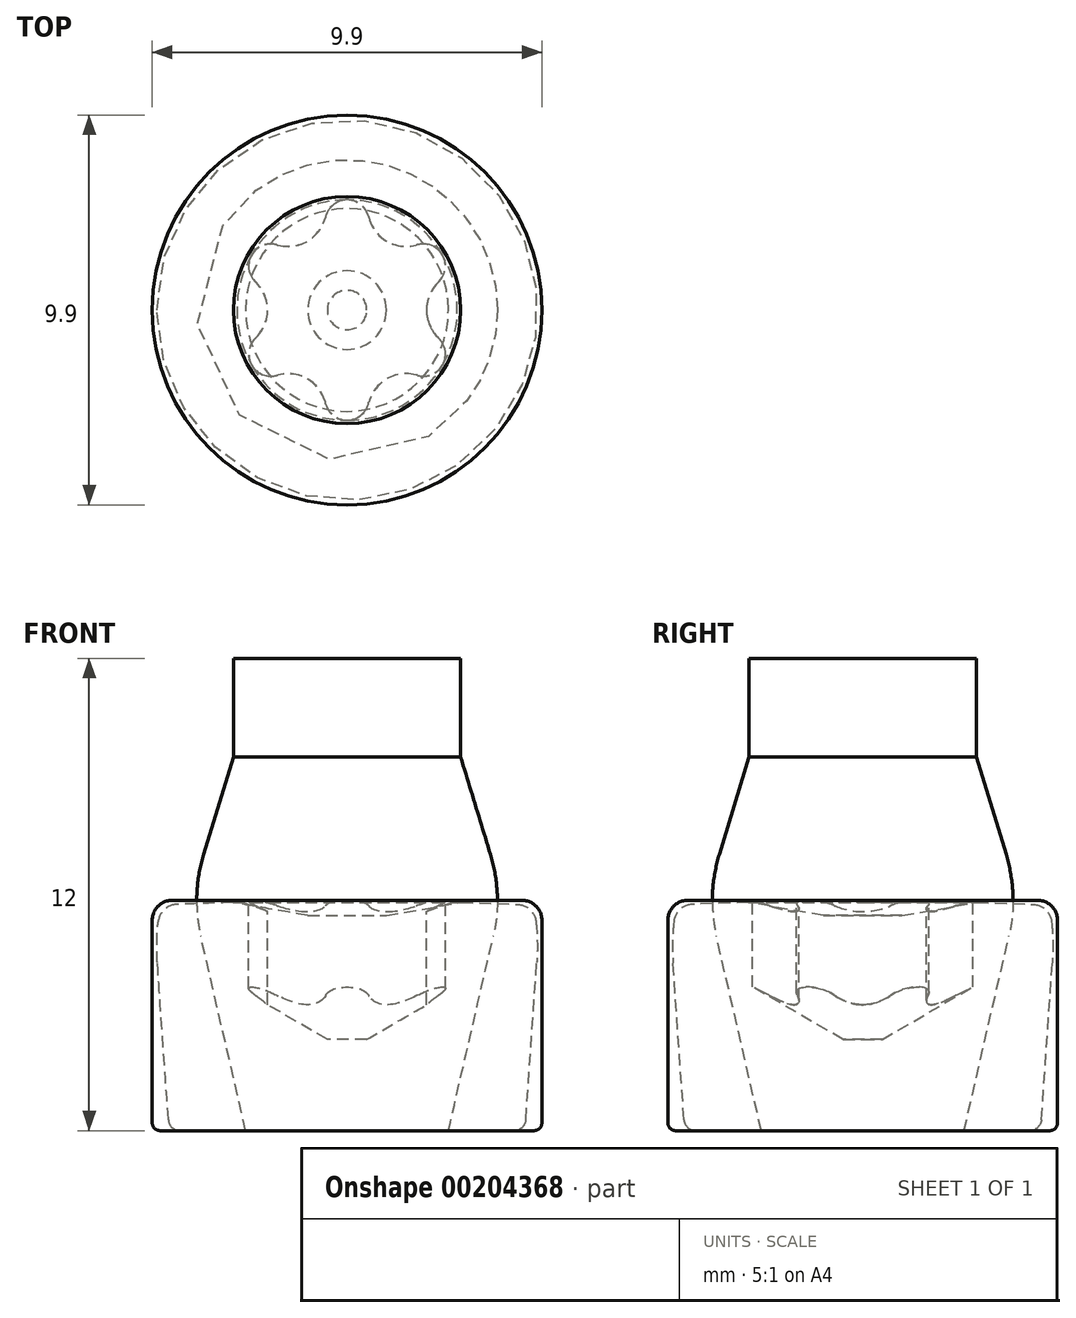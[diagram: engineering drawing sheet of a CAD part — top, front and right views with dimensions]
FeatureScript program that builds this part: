
annotation { "Feature Type Name" : "Feature", "Feature Type Description" : "" }
export const myFeature = defineFeature(function(context is Context, id is Id, definition is map)
    precondition{}
    {
        {
            var Q0;
            Q0=qCreatedBy(makeId("Front.planeOp"),FACE);
            var sketch = newSketch(context, id + "F0", { "sketchPlane" : qUnion([Q0])});
            skLineSegment(sketch, "E0", {"start": v(0, 0) * mm, "end": v(0, 2.32) * mm, "construction": true});
            skLineSegment(sketch, "E1", {"start": v(2.8, 5.85) * mm, "end": v(4.45, 5.85) * mm});
            skLineSegment(sketch, "E2", {"start": v(4.95, 5.35) * mm, "end": v(4.95, 0.2) * mm});
            skLineSegment(sketch, "E3", {"start": v(4.75, 0) * mm, "end": v(0, 0) * mm});
            skPoint(sketch, "E4.visualSharp", {"position": v(4.95, 5.85) * mm});
            skArc(sketch, "E4.filletArc", {"start": v(4.95, 5.35) * mm, "mid": v(4.8, 5.7) * mm, "end": v(4.45, 5.85) * mm});
            skPoint(sketch, "E5.visualSharp", {"position": v(4.95, 0) * mm});
            skArc(sketch, "E5.filletArc", {"start": v(4.75, 0) * mm, "mid": v(4.9, 0.06) * mm, "end": v(4.95, 0.2) * mm});
            skLineSegment(sketch, "E6", {"start": v(2.8, 5.85) * mm, "end": v(2.8, 3.65) * mm});
            skLineSegment(sketch, "E7", {"start": v(2.8, 3.65) * mm, "end": v(0.5, 2.32) * mm});
            skLineSegment(sketch, "E8", {"start": v(0.5, 2.32) * mm, "end": v(0, 2.32) * mm});
            skLineSegment(sketch, "E9", {"start": v(0, 2.32) * mm, "end": v(0, 0) * mm});
            skSolve(sketch);
        }
        {
            var Q0;
            Q0=qSketchRegion(id+"F0",true);
            var Q1;
            Q1=sQuery(id+"F0.wireOp",EDGE,"E9");
            revolve(context, id + "F1", {"entities" : qUnion([Q0]), "axis" : qUnion([Q1]), "revolveType" : RevolveType.FULL});
        }
        {
            var Q0;
            Q0=makeQuery(id+"F1.opRevolve","SWEPT_FACE",FACE,{"disambiguationData":[OSD([sQuery(id+"F0.wireOp",EDGE,"E1")])]});
            var sketch = newSketch(context, id + "F2", { "sketchPlane" : qUnion([Q0])});
            skArc(sketch, "E10", {"start": v(0.54, 2.38) * mm, "mid": v(0, 2.8) * mm, "end": v(-0.54, 2.38) * mm});
            skLineSegment(sketch, "E11", {"start": v(-0.54, 2.38) * mm, "end": v(-0.55, 2.34) * mm});
            skLineSegment(sketch, "E12", {"start": v(0.54, 2.38) * mm, "end": v(0.55, 2.34) * mm});
            skLineSegment(sketch, "E13.1.0", {"start": v(-1.8, 1.66) * mm, "end": v(-1.75, 1.65) * mm});
            skArc(sketch, "E13.1.1", {"start": v(-1.8, 1.66) * mm, "mid": v(-2.42, 1.4) * mm, "end": v(-2.34, 0.72) * mm});
            skLineSegment(sketch, "E13.1.2", {"start": v(-2.34, 0.72) * mm, "end": v(-2.3, 0.7) * mm});
            skLineSegment(sketch, "E13.2.0", {"start": v(-2.34, -0.72) * mm, "end": v(-2.3, -0.7) * mm});
            skArc(sketch, "E13.2.1", {"start": v(-2.34, -0.72) * mm, "mid": v(-2.42, -1.4) * mm, "end": v(-1.8, -1.66) * mm});
            skLineSegment(sketch, "E13.2.2", {"start": v(-1.8, -1.66) * mm, "end": v(-1.75, -1.65) * mm});
            skLineSegment(sketch, "E13.3.0", {"start": v(-0.54, -2.38) * mm, "end": v(-0.55, -2.34) * mm});
            skArc(sketch, "E13.3.1", {"start": v(-0.54, -2.38) * mm, "mid": v(0, -2.8) * mm, "end": v(0.54, -2.38) * mm});
            skLineSegment(sketch, "E13.3.2", {"start": v(0.54, -2.38) * mm, "end": v(0.55, -2.34) * mm});
            skLineSegment(sketch, "E13.4.0", {"start": v(1.8, -1.66) * mm, "end": v(1.75, -1.65) * mm});
            skArc(sketch, "E13.4.1", {"start": v(1.8, -1.66) * mm, "mid": v(2.42, -1.4) * mm, "end": v(2.34, -0.72) * mm});
            skLineSegment(sketch, "E13.4.2", {"start": v(2.34, -0.72) * mm, "end": v(2.3, -0.7) * mm});
            skLineSegment(sketch, "E13.5.0", {"start": v(2.34, 0.72) * mm, "end": v(2.3, 0.7) * mm});
            skArc(sketch, "E13.5.1", {"start": v(2.34, 0.72) * mm, "mid": v(2.42, 1.4) * mm, "end": v(1.8, 1.66) * mm});
            skLineSegment(sketch, "E13.5.2", {"start": v(1.8, 1.66) * mm, "end": v(1.75, 1.65) * mm});
            skPoint(sketch, "E13.center", {"position": v(0, 0) * mm});
            skPoint(sketch, "E14.newPointA", {"position": v(1.38, 0.81) * mm});
            skPoint(sketch, "E14.newPointB", {"position": v(-1.4, -0.8) * mm});
            skArc(sketch, "E14.filletArc", {"start": v(-1.75, 1.65) * mm, "mid": v(-1, 1.75) * mm, "end": v(-0.55, 2.34) * mm});
            skPoint(sketch, "E15.newPointA", {"position": v(-1.38, 0.8) * mm});
            skPoint(sketch, "E15.newPointB", {"position": v(1.4, -0.79) * mm});
            skArc(sketch, "E15.filletArc", {"start": v(0.55, 2.34) * mm, "mid": v(1, 1.75) * mm, "end": v(1.75, 1.65) * mm});
            skPoint(sketch, "E16.newPointA", {"position": v(0.01, -1.6) * mm});
            skPoint(sketch, "E16.newPointB", {"position": v(0, 1.6) * mm});
            skArc(sketch, "E16.filletArc", {"start": v(2.3, 0.7) * mm, "mid": v(2.02, 0) * mm, "end": v(2.3, -0.7) * mm});
            skPoint(sketch, "E17.newPointA", {"position": v(-1.38, -0.81) * mm});
            skPoint(sketch, "E17.newPointB", {"position": v(1.4, 0.8) * mm});
            skArc(sketch, "E17.filletArc", {"start": v(1.75, -1.65) * mm, "mid": v(1, -1.75) * mm, "end": v(0.55, -2.34) * mm});
            skPoint(sketch, "E18.newPointA", {"position": v(-1.4, 0.79) * mm});
            skPoint(sketch, "E18.newPointB", {"position": v(1.38, -0.8) * mm});
            skArc(sketch, "E18.filletArc", {"start": v(-0.55, -2.34) * mm, "mid": v(-1, -1.75) * mm, "end": v(-1.75, -1.65) * mm});
            skPoint(sketch, "E19.newPointA", {"position": v(-0.01, 1.6) * mm});
            skPoint(sketch, "E19.newPointB", {"position": v(0, -1.6) * mm});
            skArc(sketch, "E19.filletArc", {"start": v(-2.3, -0.7) * mm, "mid": v(-2.02, 0) * mm, "end": v(-2.3, 0.7) * mm});
            skCircle(sketch, "E20", {"center": v(0, 0) * mm, "radius": 3 * mm});
            skSolve(sketch);
        }
        {
            var Q0;
            Q0=qSketchRegion(id+"F2",true);
            var Q1;
            Q1=makeQuery(id+"F1.opRevolve","SWEPT_FACE",FACE,{"disambiguationData":[OSD([sQuery(id+"F0.wireOp",EDGE,"E7")])]});
            extrude(context, id + "F3", {"entities" : qUnion([Q0]), "operationType" : NewBodyOperationType.ADD, "endBound" : BoundingType.UP_TO_SURFACE, "oppositeDirection" : true, "endBoundEntityFace" : qUnion([Q1]), "depth" : 25 * mm, "offsetDistance" : 25 * mm});
        }
        {
            var Q0;
            Q0=makeQuery(id+"F3.boolean.opBoolean","MERGE",FACE,{"derivedFrom":[makeQuery(id+"F1.opRevolve","SWEPT_FACE",FACE,{"disambiguationData":[OSD([sQuery(id+"F0.wireOp",EDGE,"E1")])]}),makeQuery(id+"F3.opExtrude","CAP_FACE",FACE,{"disambiguationData":[OSD([sQuery(id+"F2.wireOp",EDGE,"E10"),sQuery(id+"F2.wireOp",EDGE,"E11"),sQuery(id+"F2.wireOp",EDGE,"E12"),sQuery(id+"F2.wireOp",EDGE,"E13.1.0"),sQuery(id+"F2.wireOp",EDGE,"E13.1.1"),sQuery(id+"F2.wireOp",EDGE,"E13.1.2"),sQuery(id+"F2.wireOp",EDGE,"E13.2.0"),sQuery(id+"F2.wireOp",EDGE,"E13.2.1"),sQuery(id+"F2.wireOp",EDGE,"E13.2.2"),sQuery(id+"F2.wireOp",EDGE,"E13.3.0"),sQuery(id+"F2.wireOp",EDGE,"E13.3.1"),sQuery(id+"F2.wireOp",EDGE,"E13.3.2"),sQuery(id+"F2.wireOp",EDGE,"E13.4.0"),sQuery(id+"F2.wireOp",EDGE,"E13.4.1"),sQuery(id+"F2.wireOp",EDGE,"E13.4.2"),sQuery(id+"F2.wireOp",EDGE,"E13.5.0"),sQuery(id+"F2.wireOp",EDGE,"E13.5.1"),sQuery(id+"F2.wireOp",EDGE,"E13.5.2"),sQuery(id+"F2.wireOp",EDGE,"E14.filletArc"),sQuery(id+"F2.wireOp",EDGE,"E15.filletArc"),sQuery(id+"F2.wireOp",EDGE,"E16.filletArc"),sQuery(id+"F2.wireOp",EDGE,"E17.filletArc"),sQuery(id+"F2.wireOp",EDGE,"E18.filletArc"),sQuery(id+"F2.wireOp",EDGE,"E19.filletArc"),sQuery(id+"F2.wireOp",EDGE,"E20")])],"isStart":true})]});
            var sketch = newSketch(context, id + "F4", { "sketchPlane" : qUnion([Q0])});
            skCircle(sketch, "E21", {"center": v(0, 0) * mm, "radius": 2.8 * mm});
            skSolve(sketch);
        }
        {
            var Q0;
            Q0=qSketchRegion(id+"F4",true);
            extrude(context, id + "F5", {"entities" : qUnion([Q0]), "operationType" : NewBodyOperationType.REMOVE, "oppositeDirection" : true, "depth" : 1 * mm, "hasDraft" : true, "draftAngle" : 70 * degree, "draftPullDirection" : true});
        }
        {
            var Q0;
            Q0=qCreatedBy(makeId("Front.planeOp"),FACE);
            var sketch = newSketch(context, id + "F6", { "sketchPlane" : qUnion([Q0])});
            skLineSegment(sketch, "E22", {"start": v(0, 0) * mm, "end": v(0, 12) * mm, "construction": true});
            skLineSegment(sketch, "E23", {"start": v(0, 12) * mm, "end": v(2.88, 12) * mm});
            skLineSegment(sketch, "E24", {"start": v(2.88, 12) * mm, "end": v(2.88, 9.5) * mm});
            skLineSegment(sketch, "E25", {"start": v(2.88, 9.5) * mm, "end": v(3.64, 7.02) * mm});
            skLineSegment(sketch, "E26", {"start": v(2.58, 0) * mm, "end": v(0, 0) * mm});
            skLineSegment(sketch, "E27", {"start": v(0, 12) * mm, "end": v(0, 0) * mm});
            skLineSegment(sketch, "E28", {"start": v(2.58, 0) * mm, "end": v(3.72, 4.95) * mm});
            skArc(sketch, "E29.filletArc", {"start": v(3.72, 4.95) * mm, "mid": v(3.82, 5.99) * mm, "end": v(3.64, 7.02) * mm});
            skSolve(sketch);
        }
        {
            var Q0;
            Q0=qSketchRegion(id+"F6",true);
            var Q1;
            Q1=sQuery(id+"F6.wireOp",EDGE,"E27");
            revolve(context, id + "F7", {"entities" : qUnion([Q0]), "axis" : qUnion([Q1]), "revolveType" : RevolveType.FULL});
        }
        {
            var Q0;
            Q0=qCreatedBy(makeId("Front.planeOp"),FACE);
            var sketch = newSketch(context, id + "F8", { "sketchPlane" : qUnion([Q0])});
            skLineSegment(sketch, "E30", {"start": v(0, 0) * mm, "end": v(0, 5.46) * mm});
            skLineSegment(sketch, "E31", {"start": v(4.82, 4.26) * mm, "end": v(4.54, 0.28) * mm});
            skLineSegment(sketch, "E32", {"start": v(4.24, 0) * mm, "end": v(0, 0) * mm});
            skPoint(sketch, "E33.visualSharp", {"position": v(4.52, 0) * mm});
            skArc(sketch, "E33.filletArc", {"start": v(4.24, 0) * mm, "mid": v(4.45, 0.08) * mm, "end": v(4.54, 0.28) * mm});
            skLineSegment(sketch, "E34", {"start": v(0, 5.46) * mm, "end": v(0, 0) * mm, "construction": true});
            skLineSegment(sketch, "E35", {"start": v(0, 5.46) * mm, "end": v(1, 5.46) * mm});
            skLineSegment(sketch, "E36", {"start": v(1, 5.46) * mm, "end": v(2.9, 5.8) * mm});
            skLineSegment(sketch, "E37", {"start": v(2.9, 5.8) * mm, "end": v(4.32, 5.75) * mm});
            skArc(sketch, "E38.filletArc", {"start": v(4.82, 4.26) * mm, "mid": v(4.83, 4.78) * mm, "end": v(4.8, 5.3) * mm});
            skPoint(sketch, "E39.visualSharp", {"position": v(4.74, 5.74) * mm});
            skArc(sketch, "E39.filletArc", {"start": v(4.8, 5.3) * mm, "mid": v(4.64, 5.62) * mm, "end": v(4.32, 5.75) * mm});
            skLineSegment(sketch, "E40", {"start": v(4.8, 4) * mm, "end": v(4.82, 4.26) * mm, "construction": true});
            skSolve(sketch);
        }
        {
            var Q0;
            Q0=qSketchRegion(id+"F8",true);
            var Q1;
            Q1=sQuery(id+"F8.wireOp",EDGE,"E30");
            revolve(context, id + "F9", {"entities" : qUnion([Q0]), "axis" : qUnion([Q1]), "revolveType" : RevolveType.FULL});
        }
    });
